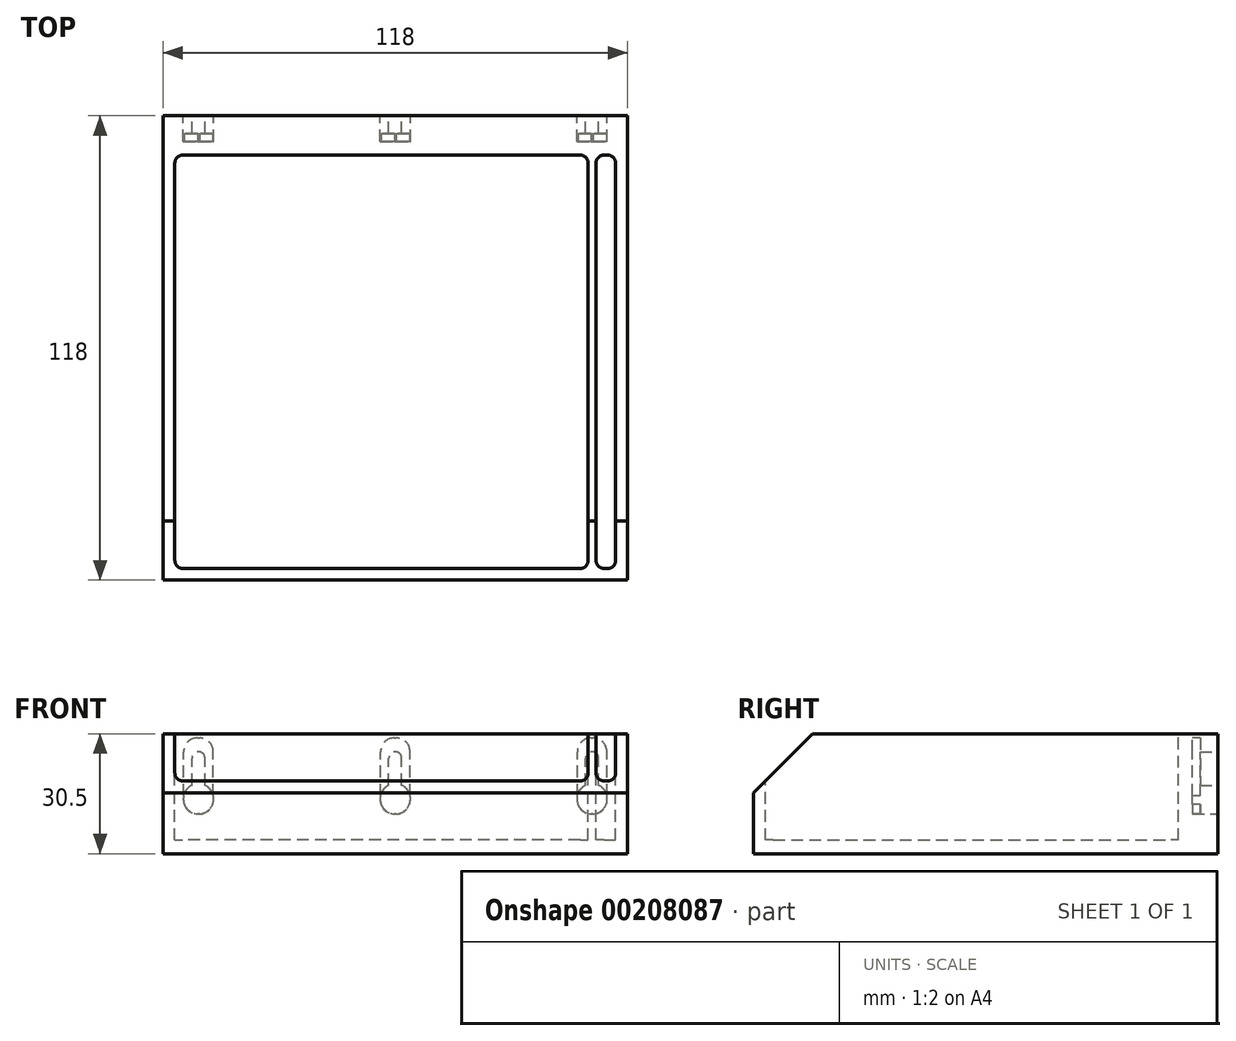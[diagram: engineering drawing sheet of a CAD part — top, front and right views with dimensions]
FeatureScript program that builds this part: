
annotation { "Feature Type Name" : "Feature", "Feature Type Description" : "" }
export const myFeature = defineFeature(function(context is Context, id is Id, definition is map)
    precondition{}
    {
        {
            var Q0;
            Q0=qCreatedBy(makeId("Top.planeOp"),FACE);
            var sketch = newSketch(context, id + "F0", { "sketchPlane" : qUnion([Q0])});
            skLineSegment(sketch, "E0.bottom", {"start": v(59, -59) * mm, "end": v(-59, -59) * mm});
            skLineSegment(sketch, "E0.top", {"start": v(59, 59) * mm, "end": v(-59, 59) * mm});
            skLineSegment(sketch, "E0.left", {"start": v(59, -59) * mm, "end": v(59, 59) * mm});
            skLineSegment(sketch, "E0.right", {"start": v(-59, -59) * mm, "end": v(-59, 59) * mm});
            skPoint(sketch, "E0.middle", {"position": v(0, 0) * mm});
            skSolve(sketch);
        }
        {
            var Q0;
            Q0 = qSketchRegion(id + "F0", true);
            extrude(context, id + "F1", {"entities" : qUnion([Q0]), "depth" : 30.5 * mm});
        }
        {
            var Q0;
            Q0=makeQuery(id+"F1.opExtrude","CAP_FACE",FACE,{"disambiguationData":[OSD([sQuery(id+"F0.wireOp",EDGE,"E0.bottom"),sQuery(id+"F0.wireOp",EDGE,"E0.top"),sQuery(id+"F0.wireOp",EDGE,"E0.left"),sQuery(id+"F0.wireOp",EDGE,"E0.right")])],"isStart":false});
            var sketch = newSketch(context, id + "F2", { "sketchPlane" : qUnion([Q0])});
            skLineSegment(sketch, "E1.bottom", {"start": v(47, -56) * mm, "end": v(-54, -56) * mm});
            skLineSegment(sketch, "E1.top", {"start": v(47, 49) * mm, "end": v(-54, 49) * mm});
            skLineSegment(sketch, "E1.left", {"start": v(49, -54) * mm, "end": v(49, 47) * mm});
            skLineSegment(sketch, "E1.right", {"start": v(-56, -54) * mm, "end": v(-56, 47) * mm});
            skPoint(sketch, "E1.middle", {"position": v(-3.5, -3.5) * mm});
            skLineSegment(sketch, "E2.bottom", {"start": v(53, -56) * mm, "end": v(54, -56) * mm});
            skLineSegment(sketch, "E2.top", {"start": v(53, 49) * mm, "end": v(54, 49) * mm});
            skLineSegment(sketch, "E2.left", {"start": v(51, -54) * mm, "end": v(51, 47) * mm});
            skLineSegment(sketch, "E2.right", {"start": v(56, -54) * mm, "end": v(56, 47) * mm});
            skPoint(sketch, "E2.middle", {"position": v(53.5, -3.5) * mm});
            skPoint(sketch, "E2.middle.positionSnap0", {"position": v(49, -3.5) * mm});
            skPoint(sketch, "E2.centerSnap0", {"position": v(49, -3.5) * mm});
            skPoint(sketch, "E3.visualSharp", {"position": v(51, 49) * mm});
            skArc(sketch, "E3.filletArc", {"start": v(53, 49) * mm, "mid": v(51.59, 48.41) * mm, "end": v(51, 47) * mm});
            skPoint(sketch, "E4.visualSharp", {"position": v(56, 49) * mm});
            skArc(sketch, "E4.filletArc", {"start": v(56, 47) * mm, "mid": v(55.41, 48.41) * mm, "end": v(54, 49) * mm});
            skPoint(sketch, "E5.visualSharp", {"position": v(51, -56) * mm});
            skArc(sketch, "E5.filletArc", {"start": v(51, -54) * mm, "mid": v(51.59, -55.41) * mm, "end": v(53, -56) * mm});
            skPoint(sketch, "E6.visualSharp", {"position": v(56, -56) * mm});
            skArc(sketch, "E6.filletArc", {"start": v(54, -56) * mm, "mid": v(55.41, -55.41) * mm, "end": v(56, -54) * mm});
            skPoint(sketch, "E7.visualSharp", {"position": v(49, -56) * mm});
            skArc(sketch, "E7.filletArc", {"start": v(47, -56) * mm, "mid": v(48.41, -55.41) * mm, "end": v(49, -54) * mm});
            skPoint(sketch, "E8.visualSharp", {"position": v(-56, -56) * mm});
            skArc(sketch, "E8.filletArc", {"start": v(-56, -54) * mm, "mid": v(-55.41, -55.41) * mm, "end": v(-54, -56) * mm});
            skPoint(sketch, "E9.visualSharp", {"position": v(-56, 49) * mm});
            skArc(sketch, "E9.filletArc", {"start": v(-54, 49) * mm, "mid": v(-55.41, 48.41) * mm, "end": v(-56, 47) * mm});
            skPoint(sketch, "E10.visualSharp", {"position": v(49, 49) * mm});
            skArc(sketch, "E10.filletArc", {"start": v(49, 47) * mm, "mid": v(48.41, 48.41) * mm, "end": v(47, 49) * mm});
            skSolve(sketch);
        }
        {
            var Q0;
            Q0 = qSketchRegion(id + "F2", true);
            extrude(context, id + "F3", {"entities" : qUnion([Q0]), "operationType" : NewBodyOperationType.REMOVE, "oppositeDirection" : true, "depth" : 27 * mm});
        }
        {
            var Q0;
            Q0=makeQuery(id+"F1.opExtrude","CAP_EDGE",EDGE,{"disambiguationData":[OSD([sQuery(id+"F0.wireOp",EDGE,"E0.bottom")])],"isStart":false});
            chamfer(context, id + "F4", {"entities" : qUnion([Q0]), "width" : 15 * mm, "tangentPropagation" : true});
        }
        {
            var Q0;
            Q0=makeQuery(id+"F1.opExtrude","SWEPT_FACE",FACE,{"disambiguationData":[OSD([sQuery(id+"F0.wireOp",EDGE,"E0.top")])]});
            var sketch = newSketch(context, id + "F5", { "sketchPlane" : qUnion([Q0])});
            skLineSegment(sketch, "E11.bottom", {"start": v(1.65, 13.93) * mm, "end": v(-1.65, 13.93) * mm});
            skLineSegment(sketch, "E11.top", {"start": v(0, 25.93) * mm, "end": v(0, 25.93) * mm});
            skLineSegment(sketch, "E11.left", {"start": v(1.65, 13.93) * mm, "end": v(1.65, 24.28) * mm});
            skLineSegment(sketch, "E11.right", {"start": v(-1.65, 13.93) * mm, "end": v(-1.65, 24.28) * mm});
            skPoint(sketch, "E11.middle", {"position": v(0, 19.93) * mm});
            skPoint(sketch, "E12.visualSharp", {"position": v(-1.65, 25.93) * mm});
            skArc(sketch, "E12.filletArc", {"start": v(0, 25.93) * mm, "mid": v(-1.17, 25.44) * mm, "end": v(-1.65, 24.28) * mm});
            skPoint(sketch, "E13.visualSharp", {"position": v(1.65, 25.93) * mm});
            skArc(sketch, "E13.filletArc", {"start": v(1.65, 24.28) * mm, "mid": v(1.17, 25.44) * mm, "end": v(0, 25.93) * mm});
            skCircle(sketch, "E14", {"center": v(0, 13.93) * mm, "radius": 3.85 * mm});
            skPoint(sketch, "E15.1.0.0", {"position": v(48.35, 25.93) * mm});
            skPoint(sketch, "E15.1.0.1", {"position": v(50, 19.93) * mm});
            skLineSegment(sketch, "E15.1.0.2", {"start": v(48.35, 13.93) * mm, "end": v(48.35, 24.28) * mm});
            skLineSegment(sketch, "E15.1.0.3", {"start": v(51.65, 13.93) * mm, "end": v(51.65, 24.28) * mm});
            skPoint(sketch, "E15.1.0.4", {"position": v(51.65, 25.93) * mm});
            skCircle(sketch, "E15.1.0.5", {"center": v(50, 13.93) * mm, "radius": 3.85 * mm});
            skLineSegment(sketch, "E15.1.0.6", {"start": v(51.65, 13.93) * mm, "end": v(48.35, 13.93) * mm});
            skArc(sketch, "E15.1.0.7", {"start": v(50, 25.93) * mm, "mid": v(48.83, 25.44) * mm, "end": v(48.35, 24.28) * mm});
            skArc(sketch, "E15.1.0.8", {"start": v(51.65, 24.28) * mm, "mid": v(51.17, 25.44) * mm, "end": v(50, 25.93) * mm});
            skLineSegment(sketch, "E15.direction1", {"start": v(-1.65, 13.93) * mm, "end": v(48.35, 13.93) * mm, "construction": true});
            skLineSegment(sketch, "E16.1.0.0", {"start": v(-51.65, 13.93) * mm, "end": v(-51.65, 24.28) * mm});
            skPoint(sketch, "E16.1.0.1", {"position": v(-50, 19.93) * mm});
            skLineSegment(sketch, "E16.1.0.2", {"start": v(-48.35, 13.93) * mm, "end": v(-48.35, 24.28) * mm});
            skCircle(sketch, "E16.1.0.3", {"center": v(-50, 13.93) * mm, "radius": 3.85 * mm});
            skPoint(sketch, "E16.1.0.4", {"position": v(-51.65, 25.93) * mm});
            skPoint(sketch, "E16.1.0.5", {"position": v(-48.35, 25.93) * mm});
            skLineSegment(sketch, "E16.1.0.6", {"start": v(-48.35, 13.93) * mm, "end": v(-51.65, 13.93) * mm});
            skArc(sketch, "E16.1.0.7", {"start": v(-50, 25.93) * mm, "mid": v(-51.17, 25.44) * mm, "end": v(-51.65, 24.28) * mm});
            skArc(sketch, "E16.1.0.8", {"start": v(-48.35, 24.28) * mm, "mid": v(-48.83, 25.44) * mm, "end": v(-50, 25.93) * mm});
            skLineSegment(sketch, "E16.direction1", {"start": v(-1.65, 13.93) * mm, "end": v(-51.65, 13.93) * mm, "construction": true});
            skSolve(sketch);
        }
        {
            var Q0;
            Q0 = qSketchRegion(id + "F5", true);
            extrude(context, id + "F6", {"entities" : qUnion([Q0]), "operationType" : NewBodyOperationType.REMOVE, "oppositeDirection" : true, "depth" : 6.5 * mm});
        }
        {
            var Q0;
            Q0=makeQuery(id+"F6.boolean.opBoolean","COPY",FACE,{"derivedFrom":makeQuery(id+"F6.opExtrude","CAP_FACE",FACE,{"disambiguationData":[OSD([sQuery(id+"F5.wireOp",EDGE,"E11.left"),sQuery(id+"F5.wireOp",EDGE,"E11.right"),sQuery(id+"F5.wireOp",EDGE,"E12.filletArc"),sQuery(id+"F5.wireOp",EDGE,"E13.filletArc"),sQuery(id+"F5.wireOp",EDGE,"E14")])],"isStart":false})});
            var sketch = newSketch(context, id + "F7", { "sketchPlane" : qUnion([Q0])});
            skLineSegment(sketch, "E17.bottom", {"start": v(0.25, 10.08) * mm, "end": v(-0.25, 10.08) * mm});
            skLineSegment(sketch, "E17.top", {"start": v(0.25, 29.43) * mm, "end": v(-0.25, 29.43) * mm});
            skLineSegment(sketch, "E17.left", {"start": v(3.75, 13.58) * mm, "end": v(3.75, 25.93) * mm});
            skLineSegment(sketch, "E17.right", {"start": v(-3.75, 13.58) * mm, "end": v(-3.75, 25.93) * mm});
            skPoint(sketch, "E17.middle", {"position": v(0, 19.75) * mm});
            skPoint(sketch, "E18.visualSharp", {"position": v(-3.75, 29.43) * mm});
            skArc(sketch, "E18.filletArc", {"start": v(-0.25, 29.43) * mm, "mid": v(-2.72, 28.4) * mm, "end": v(-3.75, 25.93) * mm});
            skPoint(sketch, "E19.visualSharp", {"position": v(3.75, 29.43) * mm});
            skArc(sketch, "E19.filletArc", {"start": v(3.75, 25.93) * mm, "mid": v(2.72, 28.4) * mm, "end": v(0.25, 29.43) * mm});
            skPoint(sketch, "E20.visualSharp", {"position": v(-3.75, 10.08) * mm});
            skArc(sketch, "E20.filletArc", {"start": v(-3.75, 13.58) * mm, "mid": v(-2.72, 11.1) * mm, "end": v(-0.25, 10.08) * mm});
            skPoint(sketch, "E21.visualSharp", {"position": v(3.75, 10.08) * mm});
            skArc(sketch, "E21.filletArc", {"start": v(0.25, 10.08) * mm, "mid": v(2.72, 11.1) * mm, "end": v(3.75, 13.58) * mm});
            skLineSegment(sketch, "E22.1.0.0", {"start": v(53.75, 13.58) * mm, "end": v(53.75, 25.93) * mm});
            skLineSegment(sketch, "E22.1.0.1", {"start": v(46.25, 13.58) * mm, "end": v(46.25, 25.93) * mm});
            skArc(sketch, "E22.1.0.2", {"start": v(49.75, 29.43) * mm, "mid": v(47.28, 28.4) * mm, "end": v(46.25, 25.93) * mm});
            skPoint(sketch, "E22.1.0.3", {"position": v(53.75, 10.08) * mm});
            skArc(sketch, "E22.1.0.4", {"start": v(53.75, 25.93) * mm, "mid": v(52.72, 28.4) * mm, "end": v(50.25, 29.43) * mm});
            skArc(sketch, "E22.1.0.5", {"start": v(46.25, 13.58) * mm, "mid": v(47.28, 11.1) * mm, "end": v(49.75, 10.08) * mm});
            skArc(sketch, "E22.1.0.6", {"start": v(50.25, 10.08) * mm, "mid": v(52.72, 11.1) * mm, "end": v(53.75, 13.58) * mm});
            skPoint(sketch, "E22.1.0.7", {"position": v(50, 19.75) * mm});
            skPoint(sketch, "E22.1.0.8", {"position": v(46.25, 10.08) * mm});
            skPoint(sketch, "E22.1.0.9", {"position": v(53.75, 29.43) * mm});
            skPoint(sketch, "E22.1.0.10", {"position": v(46.25, 29.43) * mm});
            skLineSegment(sketch, "E22.1.0.11", {"start": v(50.25, 29.43) * mm, "end": v(49.75, 29.43) * mm});
            skLineSegment(sketch, "E22.1.0.12", {"start": v(50.25, 10.08) * mm, "end": v(49.75, 10.08) * mm});
            skLineSegment(sketch, "E22.direction1", {"start": v(-3.75, 10.08) * mm, "end": v(46.25, 10.08) * mm, "construction": true});
            skArc(sketch, "E23.1.0.0", {"start": v(-46.25, 25.93) * mm, "mid": v(-47.28, 28.4) * mm, "end": v(-49.75, 29.43) * mm});
            skPoint(sketch, "E23.1.0.1", {"position": v(-53.75, 10.08) * mm});
            skArc(sketch, "E23.1.0.2", {"start": v(-50.25, 29.43) * mm, "mid": v(-52.72, 28.4) * mm, "end": v(-53.75, 25.93) * mm});
            skLineSegment(sketch, "E23.1.0.3", {"start": v(-53.75, 13.58) * mm, "end": v(-53.75, 25.93) * mm});
            skPoint(sketch, "E23.1.0.4", {"position": v(-46.25, 10.08) * mm});
            skLineSegment(sketch, "E23.1.0.5", {"start": v(-46.25, 13.58) * mm, "end": v(-46.25, 25.93) * mm});
            skArc(sketch, "E23.1.0.6", {"start": v(-53.75, 13.58) * mm, "mid": v(-52.72, 11.1) * mm, "end": v(-50.25, 10.08) * mm});
            skArc(sketch, "E23.1.0.7", {"start": v(-49.75, 10.08) * mm, "mid": v(-47.28, 11.1) * mm, "end": v(-46.25, 13.58) * mm});
            skPoint(sketch, "E23.1.0.8", {"position": v(-50, 19.75) * mm});
            skPoint(sketch, "E23.1.0.9", {"position": v(-46.25, 29.43) * mm});
            skPoint(sketch, "E23.1.0.10", {"position": v(-53.75, 29.43) * mm});
            skLineSegment(sketch, "E23.1.0.11", {"start": v(-49.75, 29.43) * mm, "end": v(-50.25, 29.43) * mm});
            skLineSegment(sketch, "E23.1.0.12", {"start": v(-49.75, 10.08) * mm, "end": v(-50.25, 10.08) * mm});
            skLineSegment(sketch, "E23.direction1", {"start": v(-3.75, 10.08) * mm, "end": v(-53.75, 10.08) * mm, "construction": true});
            skSolve(sketch);
        }
        {
            var Q0;
            Q0 = qSketchRegion(id + "F7", true);
            extrude(context, id + "F8", {"entities" : qUnion([Q0]), "operationType" : NewBodyOperationType.REMOVE, "depth" : 2 * mm});
        }
    });
